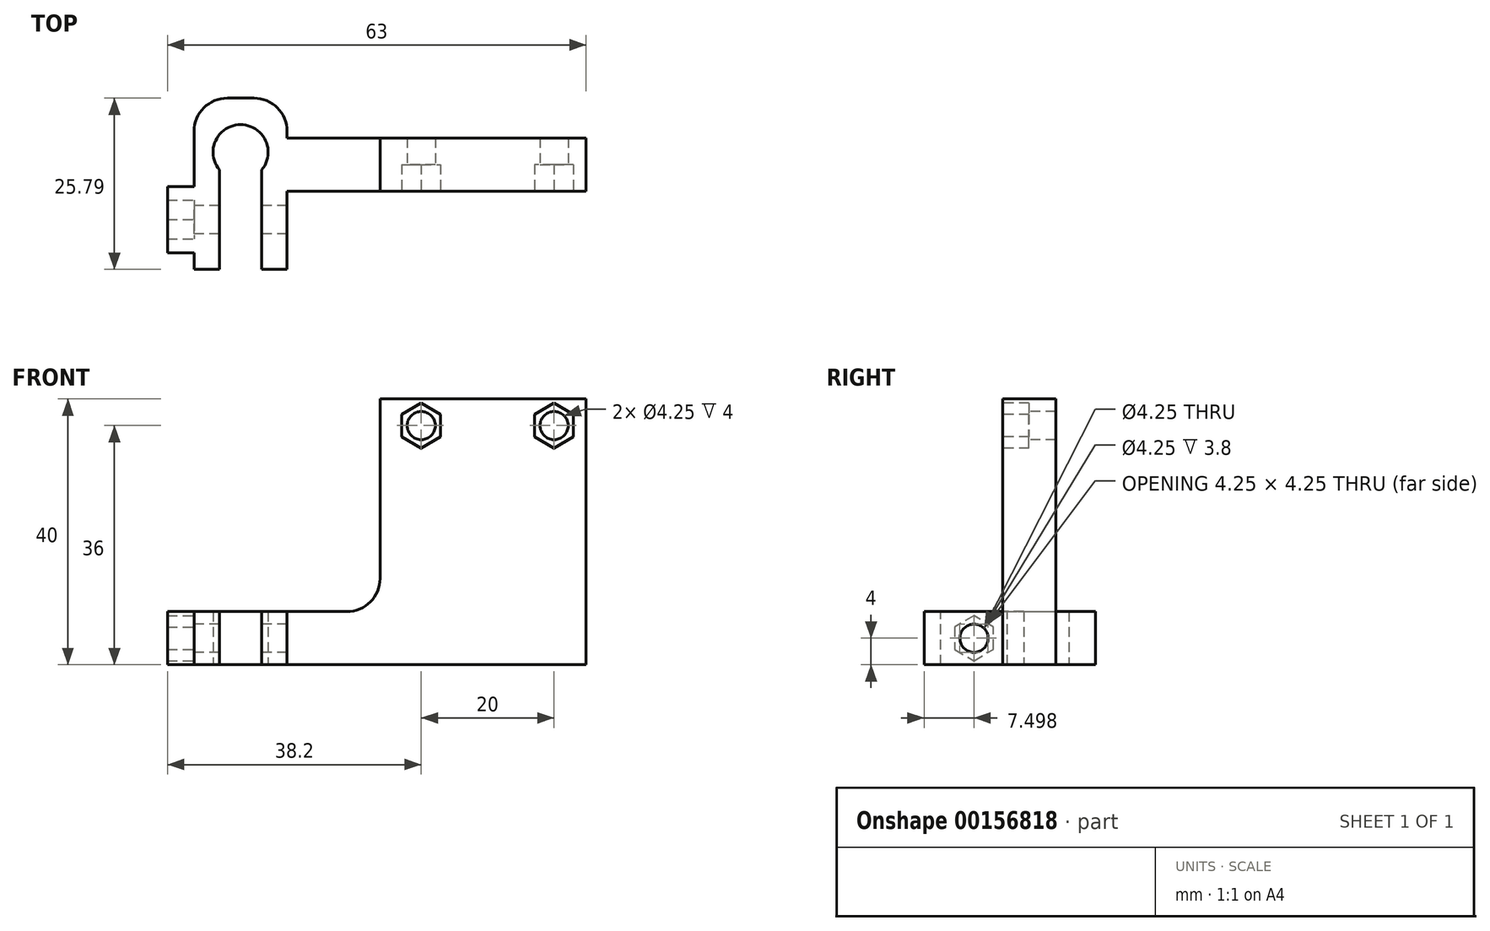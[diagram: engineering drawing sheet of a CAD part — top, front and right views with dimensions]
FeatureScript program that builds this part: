
annotation { "Feature Type Name" : "Feature", "Feature Type Description" : "" }
export const myFeature = defineFeature(function(context is Context, id is Id, definition is map)
    precondition{}
    {
        {
            var Q0;
            Q0=qCreatedBy(makeId("Top.planeOp"),FACE);
            var sketch = newSketch(context, id + "F0", { "sketchPlane" : qUnion([Q0])});
            skArc(sketch, "E0", {"start": v(3.2, -2.64) * mm, "mid": v(0, 4.15) * mm, "end": v(-3.2, -2.64) * mm});
            skLineSegment(sketch, "E1", {"start": v(-3.2, -2.64) * mm, "end": v(-3.2, -17.64) * mm});
            skLineSegment(sketch, "E2", {"start": v(-3.2, -17.64) * mm, "end": v(-7, -17.64) * mm});
            skLineSegment(sketch, "E3", {"start": v(-7, -17.64) * mm, "end": v(-7, 3.15) * mm});
            skLineSegment(sketch, "E4", {"start": v(-7, 3.15) * mm, "end": v(-7, 3.15) * mm});
            skLineSegment(sketch, "E5", {"start": v(-7, 3.15) * mm, "end": v(-7, 8.15) * mm});
            skLineSegment(sketch, "E6", {"start": v(-7, 8.15) * mm, "end": v(7, 8.15) * mm, "construction": true});
            skLineSegment(sketch, "E7", {"start": v(7, 8.15) * mm, "end": v(7, -1.85) * mm, "construction": true});
            skLineSegment(sketch, "E8", {"start": v(7, -2.65) * mm, "end": v(7, -17.64) * mm});
            skLineSegment(sketch, "E9", {"start": v(7, -17.64) * mm, "end": v(3.2, -17.64) * mm});
            skLineSegment(sketch, "E10", {"start": v(3.2, -17.64) * mm, "end": v(3.2, -2.64) * mm});
            skLineSegment(sketch, "E11", {"start": v(0, 4.15) * mm, "end": v(0, 8.15) * mm, "construction": true});
            skLineSegment(sketch, "E12", {"start": v(7, 8.15) * mm, "end": v(7, -2.65) * mm});
            skLineSegment(sketch, "E13", {"start": v(-7, 8.15) * mm, "end": v(7, 8.15) * mm});
            skLineSegment(sketch, "E14", {"start": v(7, 2.35) * mm, "end": v(7, -1.85) * mm});
            skSolve(sketch);
        }
        {
            var Q0;
            Q0=qSketchRegion(id+"F0",true);
            extrude(context, id + "F1", {"entities" : qUnion([Q0]), "endBound" : BoundingType.SYMMETRIC, "depth" : 8 * mm});
        }
        {
            var Q0;
            Q0=makeQuery(id+"F1.opExtrude","SWEPT_EDGE",EDGE,{"disambiguationData":[OSD([sQuery(id+"F0.wireOp",EDGE,"E5"),sQuery(id+"F0.wireOp",EDGE,"E6")])]});
            fillet(context, id + "F2", {"entities" : qUnion([Q0]), "radius" : 5 * mm, "tangentPropagation" : true, "allowEdgeOverflow" : false});
        }
        {
            var Q0;
            Q0=makeQuery(id+"F1.opExtrude","SWEPT_FACE",FACE,{"disambiguationData":[OSD([sQuery(id+"F0.wireOp",EDGE,"E3"),sQuery(id+"F0.wireOp",EDGE,"E5")])]});
            var sketch = newSketch(context, id + "F3", { "sketchPlane" : qUnion([Q0])});
            skCircle(sketch, "E15", {"center": v(10.14, 0) * mm, "radius": 2.12 * mm});
            skSolve(sketch);
        }
        {
            var Q0;
            Q0 = qSketchRegion(id + "F3", true);
            extrude(context, id + "F4", {"entities" : qUnion([Q0]), "operationType" : NewBodyOperationType.REMOVE, "oppositeDirection" : true, "depth" : 25 * mm});
        }
        {
            var Q0;
            Q0=makeQuery(id+"F1.opExtrude","SWEPT_FACE",FACE,{"disambiguationData":[OSD([sQuery(id+"F0.wireOp",EDGE,"E3"),sQuery(id+"F0.wireOp",EDGE,"E5")])]});
            var sketch = newSketch(context, id + "F5", { "sketchPlane" : qUnion([Q0])});
            skCircle(sketch, "E16.cCircle", {"center": v(10.14, 0) * mm, "radius": 2.93 * mm, "construction": true});
            skLineSegment(sketch, "E16.0", {"start": v(13.07, 1.69) * mm, "end": v(13.07, -1.69) * mm});
            skLineSegment(sketch, "E16.1", {"start": v(13.07, -1.69) * mm, "end": v(10.14, -3.38) * mm});
            skLineSegment(sketch, "E16.2", {"start": v(10.14, -3.38) * mm, "end": v(7.22, -1.69) * mm});
            skLineSegment(sketch, "E16.3", {"start": v(7.22, -1.69) * mm, "end": v(7.22, 1.69) * mm});
            skLineSegment(sketch, "E16.4", {"start": v(7.22, 1.69) * mm, "end": v(10.14, 3.38) * mm});
            skLineSegment(sketch, "E16.5", {"start": v(10.14, 3.38) * mm, "end": v(13.07, 1.69) * mm});
            skPoint(sketch, "E16.0.midPoint", {"position": v(13.07, 0) * mm});
            skLineSegment(sketch, "E17.bottom", {"start": v(15.14, -4) * mm, "end": v(5.14, -4) * mm});
            skLineSegment(sketch, "E17.top", {"start": v(15.14, 4) * mm, "end": v(5.14, 4) * mm});
            skLineSegment(sketch, "E17.left", {"start": v(15.14, -4) * mm, "end": v(15.14, 4) * mm});
            skLineSegment(sketch, "E17.right", {"start": v(5.14, -4) * mm, "end": v(5.14, 4) * mm});
            skSolve(sketch);
        }
        {
            var Q0;
            Q0 = qSketchRegion(id + "F5", true);
            extrude(context, id + "F6", {"entities" : qUnion([Q0]), "operationType" : NewBodyOperationType.ADD, "depth" : 4 * mm});
        }
        {
            var Q0;
            Q0=qCreatedBy(makeId("Top.planeOp"),FACE);
            var sketch = newSketch(context, id + "F7", { "sketchPlane" : qUnion([Q0])});
            skLineSegment(sketch, "E18.bottom", {"start": v(7, 2.15) * mm, "end": v(52, 2.15) * mm});
            skLineSegment(sketch, "E18.top", {"start": v(7, -5.85) * mm, "end": v(52, -5.85) * mm});
            skLineSegment(sketch, "E18.left", {"start": v(7, 2.15) * mm, "end": v(7, -5.85) * mm});
            skLineSegment(sketch, "E18.right", {"start": v(52, 2.15) * mm, "end": v(52, -5.85) * mm});
            skSolve(sketch);
        }
        {
            var Q0;
            Q0 = qSketchRegion(id + "F7", true);
            extrude(context, id + "F8", {"entities" : qUnion([Q0]), "operationType" : NewBodyOperationType.ADD, "depth" : 36 * mm});
        }
        {
            var Q0;
            Q0=makeQuery(id+"F8.opExtrude","CAP_FACE",FACE,{"disambiguationData":[OSD([sQuery(id+"F7.wireOp",EDGE,"E18.bottom"),sQuery(id+"F7.wireOp",EDGE,"E18.top"),sQuery(id+"F7.wireOp",EDGE,"E18.left"),sQuery(id+"F7.wireOp",EDGE,"E18.right")])],"isStart":true});
            var sketch = newSketch(context, id + "F9", { "sketchPlane" : qUnion([Q0])});
            skLineSegment(sketch, "E19.bottom", {"start": v(52, -2.15) * mm, "end": v(7, -2.15) * mm});
            skLineSegment(sketch, "E19.top", {"start": v(52, 5.85) * mm, "end": v(7, 5.85) * mm});
            skLineSegment(sketch, "E19.left", {"start": v(52, -2.15) * mm, "end": v(52, 5.85) * mm});
            skLineSegment(sketch, "E19.right", {"start": v(7, -2.15) * mm, "end": v(7, 5.85) * mm});
            skSolve(sketch);
        }
        {
            var Q0;
            Q0 = qSketchRegion(id + "F9", true);
            extrude(context, id + "F10", {"entities" : qUnion([Q0]), "operationType" : NewBodyOperationType.ADD, "depth" : 4 * mm});
        }
        {
            var Q0;
            Q0=makeQuery(id+"F10.boolean.opBoolean","MERGE",FACE,{"derivedFrom":[makeQuery(id+"F8.opExtrude","SWEPT_FACE",FACE,{"disambiguationData":[OSD([sQuery(id+"F7.wireOp",EDGE,"E18.top")])]}),makeQuery(id+"F10.opExtrude","SWEPT_FACE",FACE,{"disambiguationData":[OSD([sQuery(id+"F9.wireOp",EDGE,"E19.top")])]})]});
            var sketch = newSketch(context, id + "F11", { "sketchPlane" : qUnion([Q0])});
            skCircle(sketch, "E20", {"center": v(27.2, 32) * mm, "radius": 2.12 * mm});
            skCircle(sketch, "E21", {"center": v(47.2, 32) * mm, "radius": 2.12 * mm});
            skSolve(sketch);
        }
        {
            var Q0;
            Q0 = qSketchRegion(id + "F11", true);
            extrude(context, id + "F12", {"entities" : qUnion([Q0]), "operationType" : NewBodyOperationType.REMOVE, "oppositeDirection" : true, "depth" : 25 * mm});
        }
        {
            var Q0;
            Q0=makeQuery(id+"F10.boolean.opBoolean","MERGE",FACE,{"derivedFrom":[makeQuery(id+"F8.opExtrude","SWEPT_FACE",FACE,{"disambiguationData":[OSD([sQuery(id+"F7.wireOp",EDGE,"E18.top")])]}),makeQuery(id+"F10.opExtrude","SWEPT_FACE",FACE,{"disambiguationData":[OSD([sQuery(id+"F9.wireOp",EDGE,"E19.top")])]})]});
            var sketch = newSketch(context, id + "F13", { "sketchPlane" : qUnion([Q0])});
            skCircle(sketch, "E22.cCircle", {"center": v(27.2, 32) * mm, "radius": 2.93 * mm, "construction": true});
            skLineSegment(sketch, "E22.0", {"start": v(30.12, 33.69) * mm, "end": v(30.12, 30.31) * mm});
            skLineSegment(sketch, "E22.1", {"start": v(30.12, 30.31) * mm, "end": v(27.2, 28.62) * mm});
            skLineSegment(sketch, "E22.2", {"start": v(27.2, 28.62) * mm, "end": v(24.27, 30.31) * mm});
            skLineSegment(sketch, "E22.3", {"start": v(24.27, 30.31) * mm, "end": v(24.27, 33.69) * mm});
            skLineSegment(sketch, "E22.4", {"start": v(24.27, 33.69) * mm, "end": v(27.2, 35.38) * mm});
            skLineSegment(sketch, "E22.5", {"start": v(27.2, 35.38) * mm, "end": v(30.13, 33.69) * mm});
            skPoint(sketch, "E22.0.midPoint", {"position": v(30.12, 32) * mm});
            skCircle(sketch, "E23.cCircle", {"center": v(47.2, 32) * mm, "radius": 2.93 * mm, "construction": true});
            skLineSegment(sketch, "E23.0", {"start": v(44.27, 30.31) * mm, "end": v(44.27, 33.69) * mm});
            skLineSegment(sketch, "E23.1", {"start": v(44.27, 33.69) * mm, "end": v(47.2, 35.38) * mm});
            skLineSegment(sketch, "E23.2", {"start": v(47.2, 35.38) * mm, "end": v(50.12, 33.69) * mm});
            skLineSegment(sketch, "E23.3", {"start": v(50.13, 33.69) * mm, "end": v(50.13, 30.31) * mm});
            skLineSegment(sketch, "E23.4", {"start": v(50.12, 30.31) * mm, "end": v(47.2, 28.62) * mm});
            skLineSegment(sketch, "E23.5", {"start": v(47.2, 28.62) * mm, "end": v(44.27, 30.31) * mm});
            skPoint(sketch, "E23.0.midPoint", {"position": v(44.27, 32) * mm});
            skSolve(sketch);
        }
        {
            var Q0;
            Q0 = qSketchRegion(id + "F13", true);
            extrude(context, id + "F14", {"entities" : qUnion([Q0]), "operationType" : NewBodyOperationType.REMOVE, "oppositeDirection" : true, "depth" : 4 * mm});
        }
        {
            var Q0;
            Q0=makeQuery(id+"F10.boolean.opBoolean","MERGE",FACE,{"derivedFrom":[makeQuery(id+"F8.opExtrude","SWEPT_FACE",FACE,{"disambiguationData":[OSD([sQuery(id+"F7.wireOp",EDGE,"E18.bottom")])]}),makeQuery(id+"F10.opExtrude","SWEPT_FACE",FACE,{"disambiguationData":[OSD([sQuery(id+"F9.wireOp",EDGE,"E19.bottom")])]})]});
            var sketch = newSketch(context, id + "F15", { "sketchPlane" : qUnion([Q0])});
            skLineSegment(sketch, "E24.bottom", {"start": v(-7, 36) * mm, "end": v(-21, 36) * mm});
            skLineSegment(sketch, "E24.top", {"start": v(-7, 4) * mm, "end": v(-21, 4) * mm});
            skLineSegment(sketch, "E24.left", {"start": v(-7, 36) * mm, "end": v(-7, 4) * mm});
            skLineSegment(sketch, "E24.right", {"start": v(-21, 36) * mm, "end": v(-21, 4) * mm});
            skSolve(sketch);
        }
        {
            var Q0;
            Q0 = qSketchRegion(id + "F15", true);
            extrude(context, id + "F16", {"entities" : qUnion([Q0]), "operationType" : NewBodyOperationType.REMOVE, "oppositeDirection" : true, "depth" : 25 * mm});
        }
        {
            var Q0;
            Q0=makeQuery(id+"F16.boolean.opBoolean","COPY",EDGE,{"derivedFrom":makeQuery(id+"F16.opExtrude","SWEPT_EDGE",EDGE,{"disambiguationData":[OSD([sQuery(id+"F15.wireOp",EDGE,"E24.top"),sQuery(id+"F15.wireOp",EDGE,"E24.right")])]})});
            var Q1;
            Q1=makeQuery(id+"F1.opExtrude","SWEPT_EDGE",EDGE,{"disambiguationData":[OSD([sQuery(id+"F0.wireOp",EDGE,"E12"),sQuery(id+"F0.wireOp",EDGE,"E13")])]});
            fillet(context, id + "F17", {"entities" : qUnion([Q0, Q1]), "radius" : 5 * mm, "tangentPropagation" : true, "allowEdgeOverflow" : false});
        }
    });
